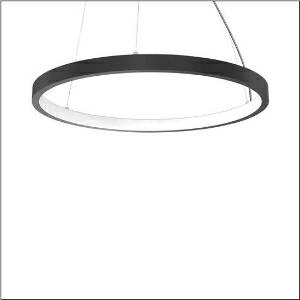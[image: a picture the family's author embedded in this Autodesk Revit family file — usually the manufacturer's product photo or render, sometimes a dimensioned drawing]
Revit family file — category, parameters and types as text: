
# Revit family: silica_r__21_ring-i_5pjbi4d1104a_67cd
name_source: partatom
category: Lighting Fixtures
units: mm (PartAtom-declared; Revit-internal decimal feet)

## family parameters
Cut with Voids When Loaded = No
Host = Face
Light Source = No
Part Type = Normal
Room Calculation Point = No
Round Connector Dimension = Use Diameter
Shared = No

## types (1)
- Silica® 21 Ring-I (1 x LED, 8460 lm, 140 W, 3000K)
    Apparent Load = 140 VA
    CIE Flux Codes = 22 48 76 50 101
    Color Rendering = 80
    Color Temperature = 3000K
    Default Elevation = 1800 mm
    Description = Silica® 21 Ring-I, suspended luminaire, of PMMA, frosted, light emission: inner ring side luminous distribution, primary light characteristic: symmetric, installation type: suspended mounting, LED, rated luminous flux: 8.460lm, luminous efficacy: 61lm/W, light colour: 830, colour temperature: 3000K, control gear: DALI 2, with terminal, 5-pole, mains connection: 230V, AC/DC, 0/50..60Hz, rated input power: 140W, housing, of extruded aluminium section, jet black (RAL 9005), diameter: 1.470mm, ceiling canopy, jet black (RAL 9005), protection rating (lamp compartment): IP40, insulation class (complete): insulation class I (protective earthing), certification: CE, impact resistance: IK02, permissible operating ambient temperature: 0..+35°C, packaging unit: 1 piece
    Height = 48 mm  [stored 0.15748 ft]
    Lamp = 1 x LED
    Lamp Light Flux = 8460 lm
    Lamp Power = 140 W
    Lamp count = 1
    Length = 1470 mm
    Luminous efficacy = 60 lm/W
    Manufacturer = Siteco
    ModVariant = No
    Model = 5PJBI4D1104A
    Mounting Place = Ceiling
    Mounting Type = Pendant
    Number of Poles = 1
    OnlyDefault = Yes
    Power Factor = 1
    Product Name = Silica® 21 Ring-I
    Product group = suspended luminaire
    ProductGroupID = 905
    Protection Class = Protection class I
    Protection Degree = IP 40
    RLX_Detail_Level = 1
    RLX_Emergency_Light_Flux = 0 lm
    RLX_Emergency_Type = 0
    RLX_Emergency_Type_DB = No
    RlxData = <blob elided: 20409 chars, md5=bc8f6ddb>
    Socket = socket
    Standby Power = 0 W
    System Light Flux = 8460 lm
    System Power = 140 W
    Type Comments = Product without accessories
    Type Image = l_1258373.jpg
    URL = http://relux.com
    VarID = ---
    Voltage = 0 V
    Weight = 0.00 kg
    Width = 0 mm  [stored 0 ft]

note: [stored X ft] marks values corroborated as IEEE doubles in the binary element streams (Revit-internal decimal feet)

## geometry (parser evidence)
native form markers: Blend x4, Sweep x12
no freeform markers — native parametric forms only
